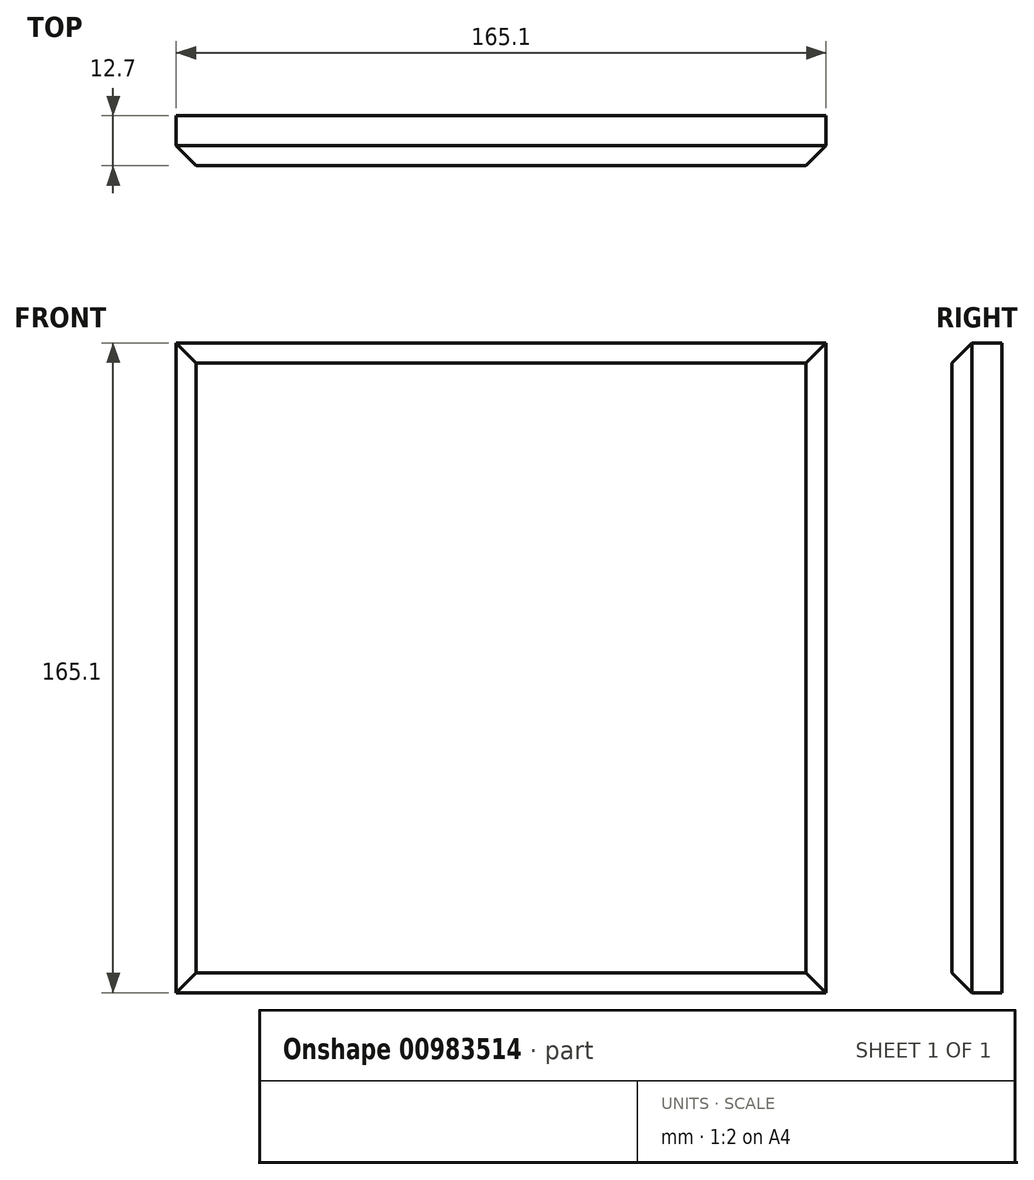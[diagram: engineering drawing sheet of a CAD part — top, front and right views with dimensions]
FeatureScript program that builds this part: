
annotation { "Feature Type Name" : "Feature", "Feature Type Description" : "" }
export const myFeature = defineFeature(function(context is Context, id is Id, definition is map)
    precondition{}
    {
        {
            var Q0;
            Q0=qCreatedBy(makeId("Front.planeOp"),FACE);
            var sketch = newSketch(context, id + "F0", { "sketchPlane" : qUnion([Q0])});
            skLineSegment(sketch, "E0.bottom", {"start": v(-142, 98.68) * mm, "end": v(23.1, 98.68) * mm});
            skLineSegment(sketch, "E0.top", {"start": v(-142, -66.42) * mm, "end": v(23.1, -66.42) * mm});
            skLineSegment(sketch, "E0.left", {"start": v(-142, 98.68) * mm, "end": v(-142, -66.42) * mm});
            skLineSegment(sketch, "E0.right", {"start": v(23.1, 98.68) * mm, "end": v(23.1, -66.42) * mm});
            skSolve(sketch);
        }
        {
            var Q0;
            Q0=makeQuery(id+"F0.imprint","IMPRINT",FACE,{"disambiguationData":[TD([[makeQuery(id+"F0.imprint","IMPRINT",EDGE,{"derivedFrom":sQuery(id+"F0.wireOp",EDGE,"E0.bottom")}),-1.0]])]});
            extrude(context, id + "F1", {"entities" : qUnion([Q0]), "depth" : 12.7 * mm, "offsetDistance" : 25.4 * mm});
        }
        {
            var Q0;
            Q0=makeQuery(id+"F1.opExtrude","CAP_EDGE",EDGE,{"disambiguationData":[OSD([sQuery(id+"F0.wireOp",EDGE,"E0.left")])],"isStart":false});
            var Q1;
            Q1=makeQuery(id+"F1.opExtrude","CAP_EDGE",EDGE,{"disambiguationData":[OSD([sQuery(id+"F0.wireOp",EDGE,"E0.bottom")])],"isStart":false});
            var Q2;
            Q2=makeQuery(id+"F1.opExtrude","CAP_EDGE",EDGE,{"disambiguationData":[OSD([sQuery(id+"F0.wireOp",EDGE,"E0.right")])],"isStart":false});
            var Q3;
            Q3=makeQuery(id+"F1.opExtrude","CAP_EDGE",EDGE,{"disambiguationData":[OSD([sQuery(id+"F0.wireOp",EDGE,"E0.top")])],"isStart":false});
            chamfer(context, id + "F2", {"entities" : qUnion([Q0, Q1, Q2, Q3]), "width" : 5.08 * mm, "tangentPropagation" : true});
        }
    });
